# Revit family: Deca_Caixa Acoplada c. Desodorizador_Axis.Living.Piano.Polo.Quadra.Unic_CD.21D
name_source: partatom
category: Plumbing Fixtures
units: mm (PartAtom-declared; Revit-internal decimal feet)

## family parameters
Cut with Voids When Loaded = No
Host = Face
Part Type = Normal
Room Calculation Point = No
Round Connector Dimension = Use Diameter
Shared = Yes

## types (1)
- CD.21D.17_Branco
    Acompanha o Produto = Kit completo duplo acionamento (mecanismo desodorizador; torre de entrada; fixações, botão acionamento duplo e função de desodorizador); Tampa própria para o kit desodorizador; Bateria; Fonte;
    Aprovado por = quattroD
    Atendimento ao Cliente = 0800-0117073
    Categoria = Bacias e bidês
    Composição Anel Vedação = -
    Composição Assento = -
    Composição Básica = -
    Composição Componente = Aço inoxidável; elastômeros e plásticos de engenharia.
    Consumo = -
    Cor Interna = 00 - Não Possui
    Cor Principal = 00 - Não Possui
    Cor Secundária = -
    Cores Componente = -
    Criado por = quattroD
    Código Pai = CD.21D
    Default Elevation = 0 m
    Description = CX ACOPL DESOD.AXIS/LIVING/PIANO/UNIC-BR
    Informações Complementares = -
    Itens de Instalação = -
    Linha = Axis/Living/Piano/Polo/Quadra/Unic
    Manufacturer = Deca
    Material = Deca_Branco
    Model = CD.21D.17
    Norma = -
    Peso Líquido (Kg) = 13542
    Pressão mín. Aquec. Acúmulo = -
    Pressão mín. Aquec. Passagem = -
    Saída de Esgoto = -
    Segmento = Banheiro Médio
    Tipo de dispositivo economizador = -
    Tipo de mecanismo utilizado = -
    Tipo de rosca de entrada = -
    Tipo de rosca de saída = -
    URL = www.deca.com.br
    Vazão na Pressão máx. (L/min) = -
    Vazão na Pressão mín. (L/min) = -

## geometry (parser evidence)
native form markers: Sweep x2
no freeform markers — native parametric forms only
